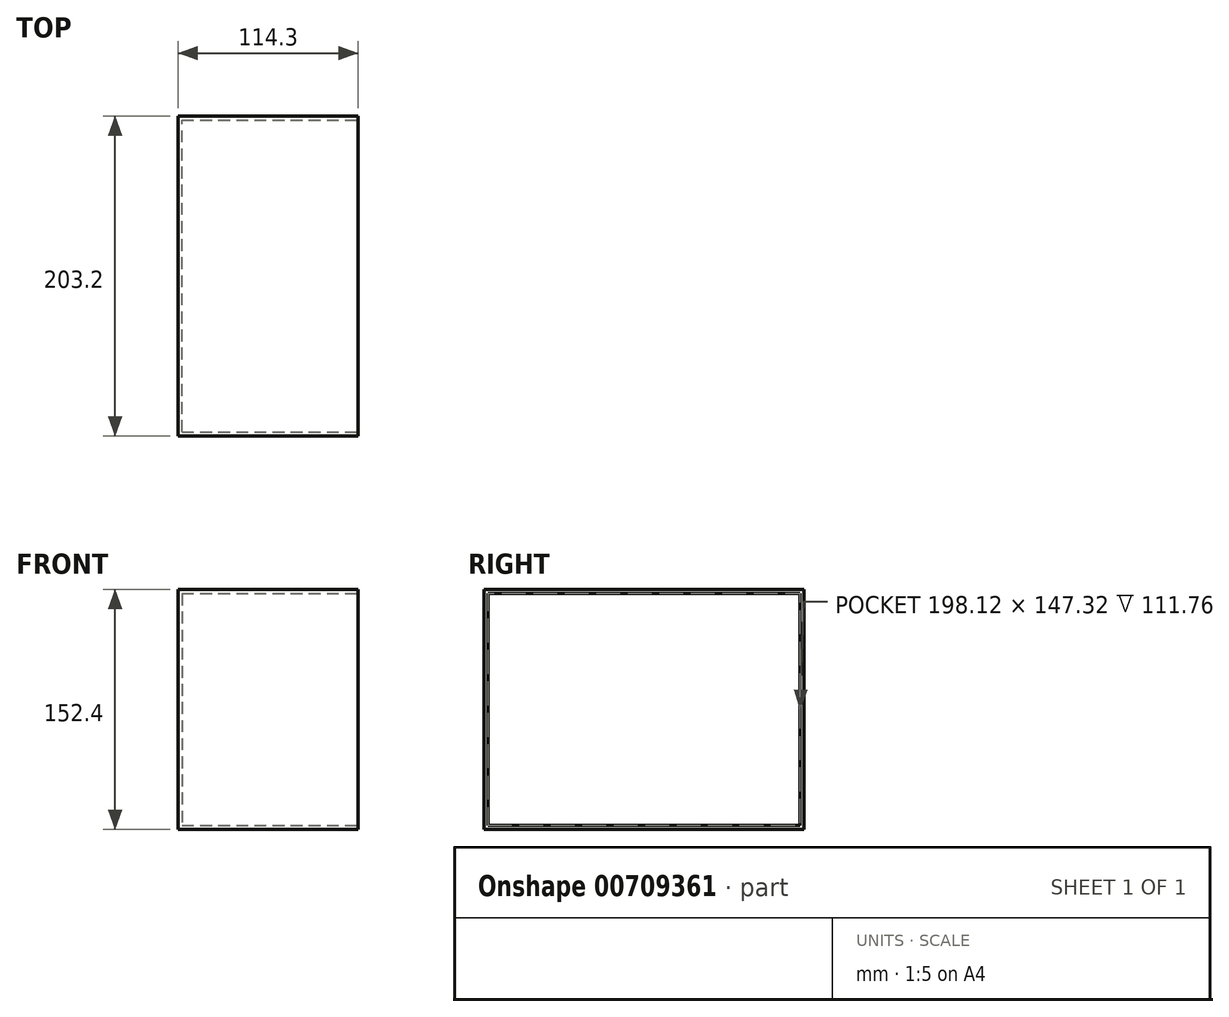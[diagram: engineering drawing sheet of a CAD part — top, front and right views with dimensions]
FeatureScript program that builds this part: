
annotation { "Feature Type Name" : "Feature", "Feature Type Description" : "" }
export const myFeature = defineFeature(function(context is Context, id is Id, definition is map)
    precondition{}
    {
        {
            var Q0;
            Q0=qCreatedBy(makeId("Front.planeOp"),FACE);
            var sketch = newSketch(context, id + "F0", { "sketchPlane" : qUnion([Q0])});
            skLineSegment(sketch, "E0.bottom", {"start": v(-56.93, 76.73) * mm, "end": v(57.37, 76.73) * mm});
            skLineSegment(sketch, "E0.top", {"start": v(-56.93, -75.67) * mm, "end": v(57.37, -75.67) * mm});
            skLineSegment(sketch, "E0.left", {"start": v(-56.93, 76.73) * mm, "end": v(-56.93, -75.67) * mm});
            skLineSegment(sketch, "E0.right", {"start": v(57.37, 76.73) * mm, "end": v(57.37, -75.67) * mm});
            skSolve(sketch);
        }
        {
            var Q0;
            Q0 = qSketchRegion(id + "F0", true);
            extrude(context, id + "F1", {"entities" : qUnion([Q0]), "depth" : 203.2 * mm, "offsetDistance" : 25.4 * mm});
        }
        {
            var Q0;
            Q0=makeQuery(id+"F1.opExtrude","SWEPT_FACE",FACE,{"disambiguationData":[OSD([sQuery(id+"F0.wireOp",EDGE,"E0.right")])]});
            shell(context, id + "F2", {"entities" : qUnion([Q0]), "thickness" : 2.54 * mm});
        }
    });
